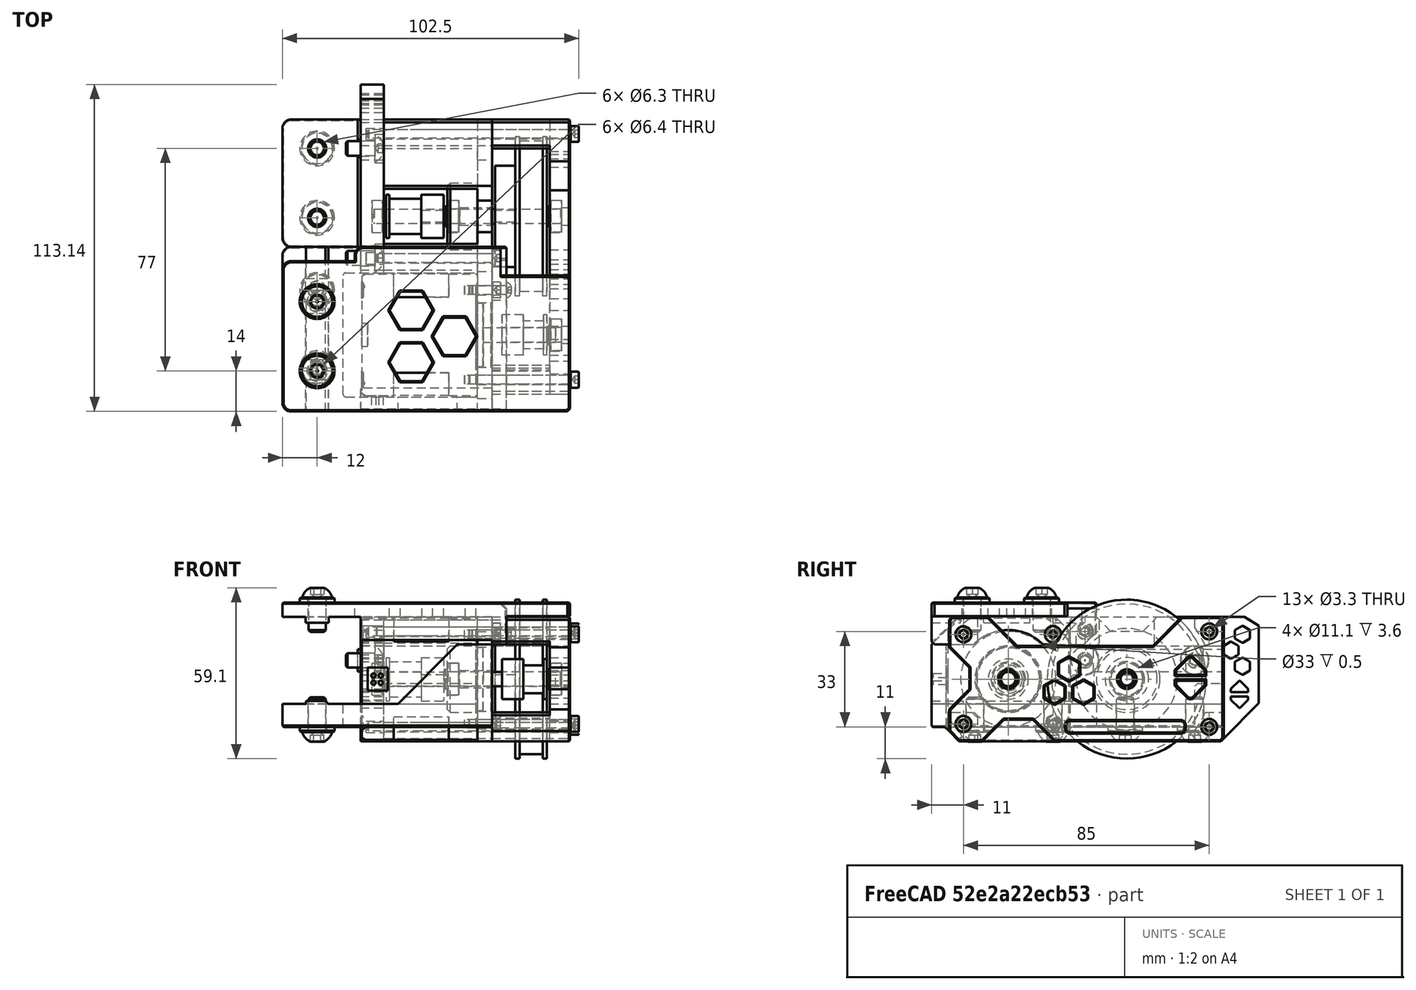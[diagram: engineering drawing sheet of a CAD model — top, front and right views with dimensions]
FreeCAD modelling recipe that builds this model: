
FCSTD DOCUMENT  (FreeCAD 0.19R24291 (Git))
Label: z-motor-right-assembly
License: Other
LicenseURL: GPL3
objects: Part::FeaturePython×21, Part::Feature×16, App::Part×1
note: 37 computed .brp shape members not serialized (recipe doc carries the construction recipe); baked Part::Feature solids carry a one-line shape summary decoded from their .brp

FEATURE [Part::Feature] Cut001024010001  label="5mm-washer005"
  shape: bbox 0.5 x 6.9 x 6.9 mm, 4 faces (baked)
FEATURE [Part::Feature] Cut001004001  label="MR115ZZ006"
  shape: bbox 4 x 11 x 11 mm, 4 faces (baked)
FEATURE [Part::Feature] Cut001024010002  label="20t-pulley001"
  shape: bbox 20 x 15 x 15 mm, 8 faces (baked)
FEATURE [Part::Feature] Cut001005001  label="MR115ZZ005"
  shape: bbox 4 x 11 x 11 mm, 4 faces (baked)
FEATURE [Part::Feature] Cut001024007001  label="5mm-washer008"
  shape: bbox 0.5 x 6.9 x 6.9 mm, 4 faces (baked)
FEATURE [Part::Feature] Cut001003001  label="MR115ZZ007"
  shape: bbox 4 x 11 x 11 mm, 4 faces (baked)
FEATURE [Part::Feature] Fusion006002011004053036004001001001  label="motor-40mm001"
  shape: bbox 67 x 47 x 42 mm, 100 faces (baked)
FEATURE [Part::Feature] Cut001024009001  label="5mm-washer006"
  shape: bbox 0.5 x 6.9 x 6.9 mm, 4 faces (baked)
FEATURE [Part::Feature] Cut001024008001  label="5mm-washer007"
  shape: bbox 0.5 x 6.9 x 6.9 mm, 4 faces (baked)
FEATURE [Part::Feature] Cut001001001  label="16t-pulley001"
  shape: bbox 15.5 x 13.9 x 13.9 mm, 8 faces (baked)
FEATURE [Part::Feature] Chamfer029006001  label="front-plate-type001"
  Placement = pos=(65.5,-1.5e-14,1e-15) rot=(0.57735,0.57735,0.57735;2.0944rad)
  shape: bbox 27 x 95 x 43 mm, 156 faces (baked)
FEATURE [Part::Feature] Fusion006002011004053036004001028003005001  label="back-plate-w-aligner001"
  shape: bbox 35 x 65.14 x 43 mm, 84 faces (baked)
FEATURE [Part::FeaturePython] Washer  label="M6-Washer"  # Fasteners workbench fastener (typed FeaturePython)
  Placement = pos=(-15,-12.5,35) rot=(0,0,1;0rad)
  diameter = 2
  invert = false
  matchOuter = true
  offset = 0
  type = 4
FEATURE [Part::FeaturePython] Washer001  label="M6-Washer011"  # Fasteners workbench fastener (typed FeaturePython)
  Placement = pos=(-15,11.5,35) rot=(0,0,1;0rad)
  diameter = 2
  invert = false
  matchOuter = true
  offset = 0
  type = 4
FEATURE [Part::FeaturePython] Washer002  label="M6-Washer009"  # Fasteners workbench fastener (typed FeaturePython)
  Placement = pos=(-15,-11.5,-8) rot=(1,0,0;3.14159rad)
  diameter = 2
  invert = true
  matchOuter = true
  offset = 0
  type = 4
FEATURE [Part::FeaturePython] Washer003  label="M6-Washer010"  # Fasteners workbench fastener (typed FeaturePython)
  Placement = pos=(-15,15.5,-8) rot=(1,0,0;3.14159rad)
  diameter = 2
  invert = true
  matchOuter = true
  offset = 0
  type = 4
FEATURE [Part::FeaturePython] Washer004  label="M6-Washer007"  # Fasteners workbench fastener (typed FeaturePython)
  Placement = pos=(-15,40.5,-8) rot=(1,0,0;3.14159rad)
  baseObject = -> Fusion006002011004053036004001028003005001 [Edge183]
  diameter = 2
  invert = true
  matchOuter = true
  offset = 0
  type = 4
FEATURE [Part::FeaturePython] Washer005  label="M6-Washer008"  # Fasteners workbench fastener (typed FeaturePython)
  Placement = pos=(-15,64.5,-8) rot=(1,0,0;3.14159rad)
  baseObject = -> Fusion006002011004053036004001028003005001 [Edge185]
  diameter = 2
  invert = true
  matchOuter = true
  offset = 0
  type = 4
FEATURE [Part::FeaturePython] Screw  label="M3x70-Screw"  # Fasteners workbench fastener (typed FeaturePython)
  Placement = pos=(72.5,69.5,-8) rot=(0,1,0;1.5708rad)
  baseObject = -> Chamfer029006001 [Edge22]
  diameter = 4
  invert = false
  length = 10
  lengthCustom = 70
  matchOuter = true
  offset = 0
  thread = false
  type = 33
FEATURE [Part::FeaturePython] Screw001  label="M3x35-Screw"  # Fasteners workbench fastener (typed FeaturePython)
  Placement = pos=(72.5,-15.5,-7) rot=(0,1,0;1.5708rad)
  baseObject = -> Chamfer029006001 [Edge26]
  diameter = 4
  invert = false
  length = 10
  lengthCustom = 35
  matchOuter = true
  offset = 0
  thread = false
  type = 33
FEATURE [Part::FeaturePython] Screw002  label="M3x35-Screw001"  # Fasteners workbench fastener (typed FeaturePython)
  Placement = pos=(72.5,-15.5,24) rot=(0,1,0;1.5708rad)
  baseObject = -> Chamfer029006001 [Edge24]
  diameter = 4
  invert = false
  length = 10
  lengthCustom = 35
  matchOuter = true
  offset = 0
  thread = false
  type = 33
FEATURE [Part::FeaturePython] Screw003  label="M3x70-Screw001"  # Fasteners workbench fastener (typed FeaturePython)
  Placement = pos=(72.5,69.5,25) rot=(0,1,0;1.5708rad)
  baseObject = -> Chamfer029006001 [Edge23]
  diameter = 4
  invert = false
  length = 10
  lengthCustom = 70
  matchOuter = true
  offset = 0
  thread = false
  type = 33
FEATURE [Part::FeaturePython] Screw004  label="M5x10-Screw"  # Fasteners workbench fastener (typed FeaturePython)
  Placement = pos=(5,26.5,15) rot=(0,1,0;1.5708rad)
  baseObject = -> Fusion006002011004053036004001028003005001 [Edge223]
  diameter = 3
  invert = false
  length = 1
  lengthCustom = 10
  matchOuter = true
  offset = 0
  thread = false
  type = 39
FEATURE [Part::FeaturePython] Screw005  label="M5x10-Screw001"  # Fasteners workbench fastener (typed FeaturePython)
  Placement = pos=(5,64.5,15) rot=(0,1,0;1.5708rad)
  baseObject = -> Fusion006002011004053036004001028003005001 [Edge90]
  diameter = 3
  invert = false
  length = 1
  lengthCustom = 10
  matchOuter = true
  offset = 0
  thread = false
  type = 39
FEATURE [Part::FeaturePython] Screw006  label="M3x8-Screw"  # Fasteners workbench fastener (typed FeaturePython)
  Placement = pos=(45.5,15.5,-7) rot=(0,1,0;1.5708rad)
  diameter = 4
  invert = false
  length = 10
  lengthCustom = 8
  matchOuter = true
  offset = 0
  thread = false
  type = 33
FEATURE [Part::FeaturePython] Screw007  label="M3x12-Screw"  # Fasteners workbench fastener (typed FeaturePython)
  Placement = pos=(50.5,15.5,24) rot=(0,1,0;1.5708rad)
  diameter = 1
  invert = false
  length = 3
  lengthCustom = 12
  matchOuter = true
  offset = 0
  thread = false
  type = 39
FEATURE [Part::FeaturePython] Screw008  label="M6x12-Screw"  # Fasteners workbench fastener (typed FeaturePython)
  Placement = pos=(-15,11.5,36.8) rot=(0,0,1;0rad)
  baseObject = -> Washer001 [Edge1]
  diameter = 4
  invert = false
  length = 1
  lengthCustom = 12
  matchOuter = true
  offset = 0
  thread = false
  type = 39
FEATURE [Part::FeaturePython] Screw009  label="M6x12-Screw007"  # Fasteners workbench fastener (typed FeaturePython)
  Placement = pos=(-15,-12.5,36.8) rot=(0,0,1;0rad)
  baseObject = -> Washer [Edge1]
  diameter = 4
  invert = false
  length = 1
  lengthCustom = 12
  matchOuter = true
  offset = 0
  thread = false
  type = 39
FEATURE [Part::FeaturePython] Screw010  label="M6x12-Screw002"  # Fasteners workbench fastener (typed FeaturePython)
  Placement = pos=(-15,64.5,-9.8) rot=(1,0,0;3.14159rad)
  baseObject = -> Washer005 [Edge1]
  diameter = 4
  invert = false
  length = 1
  lengthCustom = 12
  matchOuter = true
  offset = 0
  thread = false
  type = 39
FEATURE [Part::FeaturePython] Screw011  label="M6x12-Screw003"  # Fasteners workbench fastener (typed FeaturePython)
  Placement = pos=(-15,40.5,-9.8) rot=(1,0,0;3.14159rad)
  baseObject = -> Washer004 [Edge1]
  diameter = 4
  invert = false
  length = 1
  lengthCustom = 12
  matchOuter = true
  offset = 0
  thread = false
  type = 39
FEATURE [Part::FeaturePython] Screw012  label="M6x12-Screw006"  # Fasteners workbench fastener (typed FeaturePython)
  Placement = pos=(-15,15.5,-9.8) rot=(1,0,0;3.14159rad)
  baseObject = -> Washer003 [Edge1]
  diameter = 4
  invert = false
  length = 1
  lengthCustom = 12
  matchOuter = true
  offset = 0
  thread = false
  type = 39
FEATURE [Part::FeaturePython] Screw013  label="M6x12-Screw005"  # Fasteners workbench fastener (typed FeaturePython)
  Placement = pos=(-15,-11.5,-9.8) rot=(1,0,0;3.14159rad)
  baseObject = -> Washer002 [Edge1]
  diameter = 4
  invert = false
  length = 1
  lengthCustom = 12
  matchOuter = true
  offset = 0
  thread = false
  type = 39
FEATURE [Part::Feature] Cut001024014003001001  label="z-motor-plate-r004"
  shape: bbox 72.5 x 101 x 43 mm, 85 faces (baked)
FEATURE [Part::FeaturePython] Screw014  label="M3x40-Screw"  # Fasteners workbench fastener (typed FeaturePython)
  Placement = pos=(45.5,26.5,25) rot=(0,1,0;1.5708rad)
  baseObject = -> Cut001024014003001001 [Edge95]
  diameter = 4
  invert = false
  length = 10
  lengthCustom = 40
  matchOuter = true
  offset = 0
  thread = false
  type = 33
FEATURE [Part::Feature] Cut001024014003001002002  label="80-t-mellow"
  Placement = pos=(64.5,41,8.5) rot=(0,-1,0;1.5708rad)
  shape: bbox 18 x 55 x 55 mm, 10 faces (baked)
FEATURE [Part::Feature] Chamfer029006005001
  shape: bbox 99.5 x 57 x 14.5 mm, 102 faces (baked)
FEATURE [Part::Feature] Body002  label="5x65-shaft"
  Placement = pos=(4.5,41,8.5) rot=(0,0,1;0rad)
  shape: bbox 65 x 5 x 5 mm, 11 faces (baked)
FEATURE [App::Part] Part  label="z-motor-right"
  Group = -> [Cut001024010001,Cut001004001,Cut001024010002,Cut001005001,Cut001024007001,Cut001003001,Fusion006002011004053036004001001001,Cut001024009001,Cut001024008001,Cut001001001,Chamfer029006001,Fusion006002011004053036004001028003005001,Washer001,Screw007,Screw008,Screw009,Washer,Screw013,Screw012,Screw006,Washer003,Washer002,Screw010,Washer005,Screw004,Screw005,Screw011,Washer004,Screw001,Screw002,+7 more]
  Origin = -> Origin
